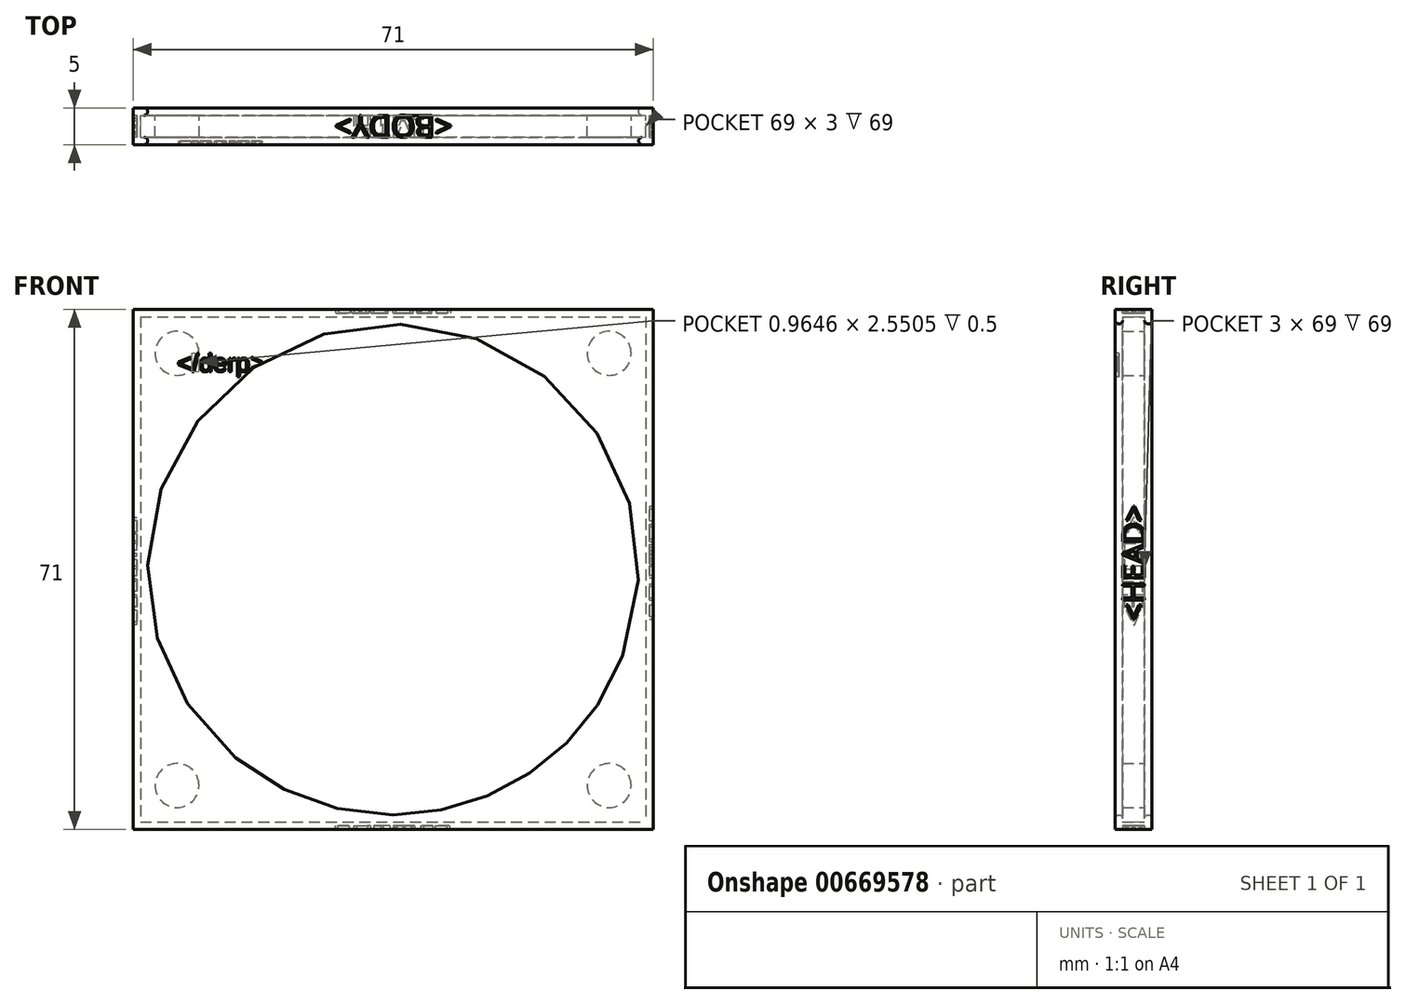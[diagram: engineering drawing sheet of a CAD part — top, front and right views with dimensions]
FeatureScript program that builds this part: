
annotation { "Feature Type Name" : "Feature", "Feature Type Description" : "" }
export const myFeature = defineFeature(function(context is Context, id is Id, definition is map)
    precondition{}
    {
        {
            var Q0;
            Q0=qCreatedBy(makeId("Front.planeOp"),FACE);
            var sketch = newSketch(context, id + "F0", { "sketchPlane" : qUnion([Q0])});
            skLineSegment(sketch, "E0.bottom", {"start": v(-35.5, 35.5) * mm, "end": v(35.5, 35.5) * mm});
            skLineSegment(sketch, "E0.top", {"start": v(-35.5, -35.5) * mm, "end": v(35.5, -35.5) * mm});
            skLineSegment(sketch, "E0.left", {"start": v(-35.5, 35.5) * mm, "end": v(-35.5, -35.5) * mm});
            skLineSegment(sketch, "E0.right", {"start": v(35.5, 35.5) * mm, "end": v(35.5, -35.5) * mm});
            skPoint(sketch, "E0.middle", {"position": v(0, 0) * mm});
            skCircle(sketch, "E1", {"center": v(0, 0) * mm, "radius": 33.5 * mm});
            skSolve(sketch);
        }
        {
            var Q0;
            Q0=makeQuery(id+"F0.imprint","IMPRINT",FACE,{"disambiguationData":[TD([[makeQuery(id+"F0.imprint","IMPRINT",EDGE,{"derivedFrom":sQuery(id+"F0.wireOp",EDGE,"E0.bottom")}),-1.0]])]});
            extrude(context, id + "F1", {"entities" : qUnion([Q0]), "depth" : 5 * mm, "offsetDistance" : 25 * mm});
        }
        {
            var Q0;
            Q0=makeQuery(id+"F1.opExtrude","CAP_FACE",FACE,{"disambiguationData":[OSD([sQuery(id+"F0.wireOp",EDGE,"E0.bottom"),sQuery(id+"F0.wireOp",EDGE,"E0.top"),sQuery(id+"F0.wireOp",EDGE,"E0.left"),sQuery(id+"F0.wireOp",EDGE,"E0.right"),sQuery(id+"F0.wireOp",EDGE,"E1")])],"isStart":false});
            var sketch = newSketch(context, id + "F2", { "sketchPlane" : qUnion([Q0])});
            skText(sketch, "E2", { "text": "</derp>", "fontName": "Arimo-Regular.ttf"});
            const initialGuessF2  = {"E2": [-0.0295, 0.027, 1, 0, 0.0025]};
            skSetInitialGuess(sketch, initialGuessF2);
            skSolve(sketch);
        }
        {
            var Q0;
            Q0=makeQuery(id+"F1.opExtrude","SWEPT_FACE",FACE,{"disambiguationData":[OSD([sQuery(id+"F0.wireOp",EDGE,"E0.top")])]});
            var sketch = newSketch(context, id + "F3", { "sketchPlane" : qUnion([Q0])});
            skText(sketch, "E3", { "text": "<HTML>", "fontName": "OpenSans-Regular.ttf"});
            const initialGuessF3  = {"E3": [-0.00816, 0.001, 1, 0, 0.003]};
            skSetInitialGuess(sketch, initialGuessF3);
            skSolve(sketch);
        }
        {
            var Q0;
            Q0=makeQuery(id+"F1.opExtrude","SWEPT_FACE",FACE,{"disambiguationData":[OSD([sQuery(id+"F0.wireOp",EDGE,"E1")])]});
            var Q1;
            Q1=makeQuery(id+"F1.opExtrude","SWEPT_BODY",BODY,{"disambiguationData":[OSD([sQuery(id+"F0.wireOp",EDGE,"E0.bottom"),sQuery(id+"F0.wireOp",EDGE,"E0.top"),sQuery(id+"F0.wireOp",EDGE,"E0.left"),sQuery(id+"F0.wireOp",EDGE,"E0.right"),sQuery(id+"F0.wireOp",EDGE,"E1")])]});
            shell(context, id + "F4", {"entities" : qUnion([Q0]), "parts" : qUnion([Q1]), "thickness" : 1 * mm});
        }
        {
            var Q0;
            Q0=makeQuery(id+"F1.opExtrude","CAP_EDGE",EDGE,{"disambiguationData":[OSD([sQuery(id+"F0.wireOp",EDGE,"E1")])],"isStart":false});
            var Q1;
            {var subQ0=sQuery(id+"F0.wireOp",EDGE,"E1");Q1=makeQuery(id+"F4.opShell","OFFSET_EDGE",EDGE,{"disambiguationData":[OSD([subQ0]),TDD([makeQuery(id+"F1.opExtrude","CAP_EDGE",EDGE,{"disambiguationData":[OSD([subQ0])],"isStart":false})])]});}
            var Q2;
            {var subQ0=sQuery(id+"F0.wireOp",EDGE,"E1");Q2=makeQuery(id+"F4.opShell","OFFSET_EDGE",EDGE,{"disambiguationData":[OSD([subQ0]),TDD([makeQuery(id+"F1.opExtrude","CAP_EDGE",EDGE,{"disambiguationData":[OSD([subQ0])],"isStart":true})])]});}
            var Q3;
            Q3=makeQuery(id+"F1.opExtrude","CAP_EDGE",EDGE,{"disambiguationData":[OSD([sQuery(id+"F0.wireOp",EDGE,"E1")])],"isStart":true});
            fillet(context, id + "F5", {"entities" : qUnion([Q0, Q1, Q2, Q3]), "radius" : .5 * mm, "tangentPropagation" : true, "allowEdgeOverflow" : false});
        }
        {
            var Q0;
            Q0=qCreatedBy(makeId("Front.planeOp"),FACE);
            var sketch = newSketch(context, id + "F6", { "sketchPlane" : qUnion([Q0])});
            skCircle(sketch, "E4", {"center": v(-29.5, -29.5) * mm, "radius": 3 * mm});
            skPoint(sketch, "E4.first.point", {"position": v(-31.03, -32.08) * mm});
            skPoint(sketch, "E4.second.point", {"position": v(-26.84, -28.12) * mm});
            skPoint(sketch, "E4.third.point", {"position": v(-31.47, -27.23) * mm});
            skCircle(sketch, "E5", {"center": v(-29.5, 29.5) * mm, "radius": 3 * mm});
            skPoint(sketch, "E5.first.point", {"position": v(-31.58, 27.34) * mm});
            skPoint(sketch, "E5.second.point", {"position": v(-27.67, 31.88) * mm});
            skPoint(sketch, "E5.third.point", {"position": v(-29.22, 32.49) * mm});
            skCircle(sketch, "E6", {"center": v(29.5, -29.5) * mm, "radius": 3 * mm});
            skPoint(sketch, "E6.first.point", {"position": v(27.16, -31.38) * mm});
            skPoint(sketch, "E6.second.point", {"position": v(31.19, -27.02) * mm});
            skPoint(sketch, "E6.third.point", {"position": v(29.18, -26.52) * mm});
            skCircle(sketch, "E7", {"center": v(29.5, 29.5) * mm, "radius": 3 * mm});
            skPoint(sketch, "E7.first.point", {"position": v(27.44, 27.32) * mm});
            skPoint(sketch, "E7.second.point", {"position": v(29.78, 32.49) * mm});
            skPoint(sketch, "E7.third.point", {"position": v(30.78, 26.79) * mm});
            skSolve(sketch);
        }
        {
            var Q0;
            Q0 = qSketchRegion(id + "F6", true);
            var Q1;
            Q1=makeQuery(id+"F1.opExtrude","CAP_FACE",FACE,{"disambiguationData":[OSD([sQuery(id+"F0.wireOp",EDGE,"E0.bottom"),sQuery(id+"F0.wireOp",EDGE,"E0.top"),sQuery(id+"F0.wireOp",EDGE,"E0.left"),sQuery(id+"F0.wireOp",EDGE,"E0.right"),sQuery(id+"F0.wireOp",EDGE,"E1")])],"isStart":false});
            extrude(context, id + "F7", {"entities" : qUnion([Q0]), "operationType" : NewBodyOperationType.ADD, "endBound" : BoundingType.UP_TO_SURFACE, "depth" : 25 * mm, "endBoundEntityFace" : qUnion([Q1]), "offsetDistance" : 25 * mm});
        }
        {
            var Q0;
            Q0 = qSketchRegion(id + "F2", true);
            extrude(context, id + "F8", {"entities" : qUnion([Q0]), "operationType" : NewBodyOperationType.REMOVE, "oppositeDirection" : true, "depth" : .5 * mm, "offsetDistance" : 25 * mm});
        }
        {
            var Q0;
            Q0 = qSketchRegion(id + "F3", true);
            extrude(context, id + "F9", {"entities" : qUnion([Q0]), "operationType" : NewBodyOperationType.REMOVE, "oppositeDirection" : true, "depth" : .5 * mm, "offsetDistance" : 25 * mm});
        }
        {
            var Q0;
            Q0=makeQuery(id+"F1.opExtrude","SWEPT_FACE",FACE,{"disambiguationData":[OSD([sQuery(id+"F0.wireOp",EDGE,"E0.right")])]});
            var sketch = newSketch(context, id + "F10", { "sketchPlane" : qUnion([Q0])});
            skText(sketch, "E8", { "text": "<HEAD>", "fontName": "OpenSans-Regular.ttf"});
            const initialGuessF10  = {"E8": [-0.001, -0.007, 0, 1, 0.003]};
            skSetInitialGuess(sketch, initialGuessF10);
            skSolve(sketch);
        }
        {
            var Q0;
            Q0 = qSketchRegion(id + "F10", true);
            extrude(context, id + "F11", {"entities" : qUnion([Q0]), "operationType" : NewBodyOperationType.REMOVE, "oppositeDirection" : true, "depth" : .5 * mm, "offsetDistance" : 25 * mm});
        }
        {
            var Q0;
            Q0=makeQuery(id+"F1.opExtrude","SWEPT_FACE",FACE,{"disambiguationData":[OSD([sQuery(id+"F0.wireOp",EDGE,"E0.bottom")])]});
            var sketch = newSketch(context, id + "F12", { "sketchPlane" : qUnion([Q0])});
            skText(sketch, "E9", { "text": "<BODY>", "fontName": "OpenSans-Regular.ttf"});
            const initialGuessF12  = {"E9": [0.00807, -0.001, -1, 0, 0.003]};
            skSetInitialGuess(sketch, initialGuessF12);
            skSolve(sketch);
        }
        {
            var Q0;
            Q0 = qSketchRegion(id + "F12", true);
            extrude(context, id + "F13", {"entities" : qUnion([Q0]), "operationType" : NewBodyOperationType.REMOVE, "oppositeDirection" : true, "depth" : .5 * mm, "offsetDistance" : 25 * mm});
        }
        {
            var Q0;
            Q0=makeQuery(id+"F1.opExtrude","SWEPT_FACE",FACE,{"disambiguationData":[OSD([sQuery(id+"F0.wireOp",EDGE,"E0.left")])]});
            var sketch = newSketch(context, id + "F14", { "sketchPlane" : qUnion([Q0])});
            skText(sketch, "E10", { "text": "<TITLE>", "fontName": "OpenSans-Regular.ttf"});
            const initialGuessF14  = {"E10": [0.001, 0.00725, 0, -1, 0.003]};
            skSetInitialGuess(sketch, initialGuessF14);
            skSolve(sketch);
        }
        {
            var Q0;
            Q0 = qSketchRegion(id + "F14", true);
            extrude(context, id + "F15", {"entities" : qUnion([Q0]), "operationType" : NewBodyOperationType.REMOVE, "oppositeDirection" : true, "depth" : .5 * mm, "offsetDistance" : 25 * mm});
        }
    });
